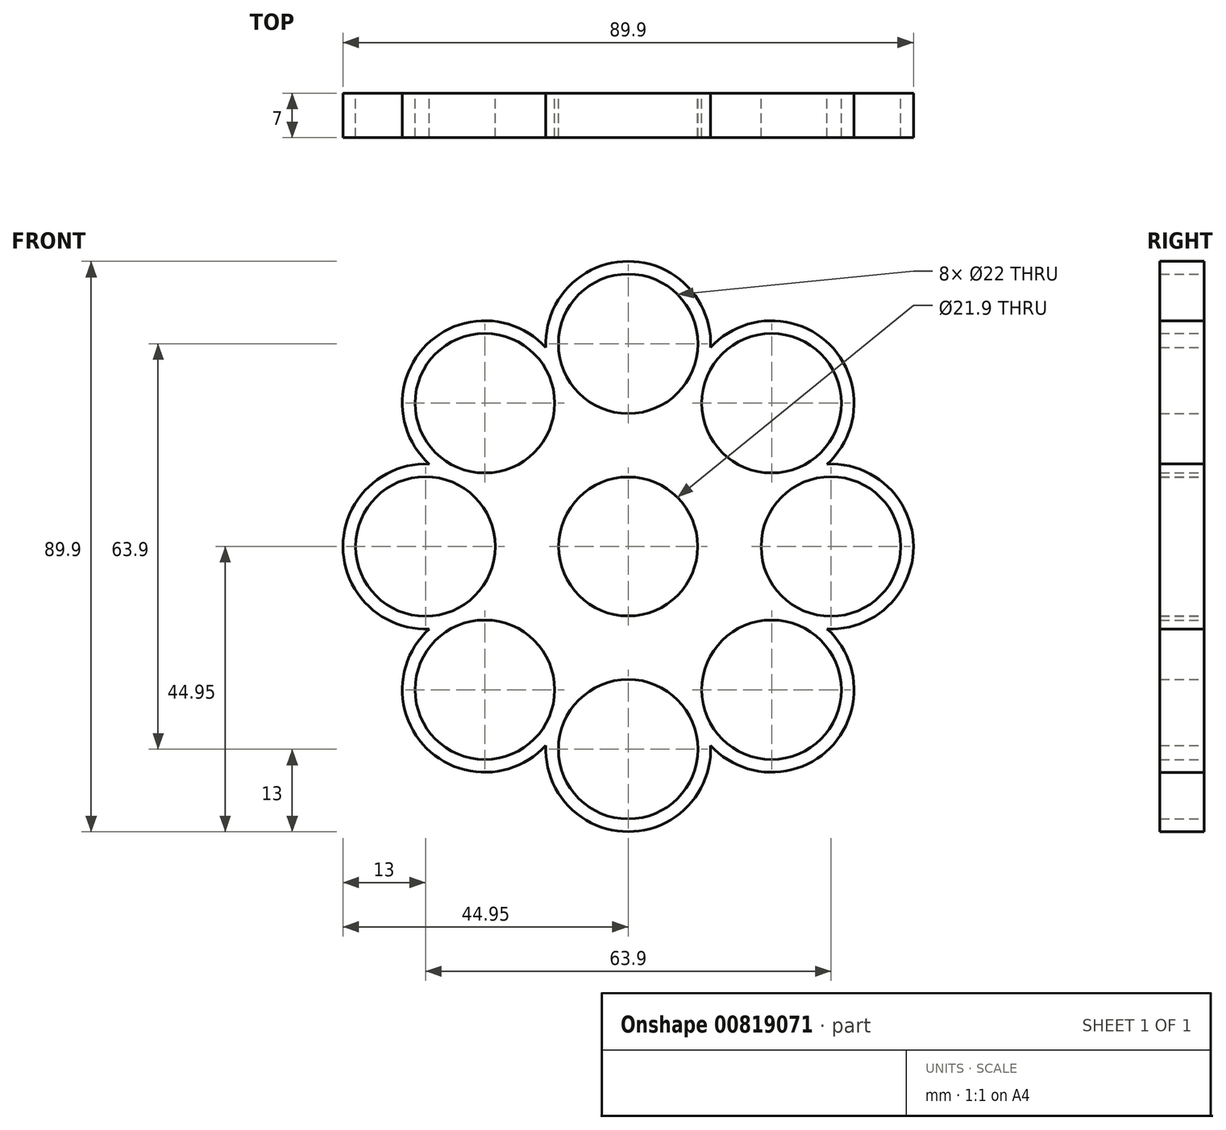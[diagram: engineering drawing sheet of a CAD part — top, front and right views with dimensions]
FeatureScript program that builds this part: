
annotation { "Feature Type Name" : "Feature", "Feature Type Description" : "" }
export const myFeature = defineFeature(function(context is Context, id is Id, definition is map)
    precondition{}
    {
        {
            var Q0;
            Q0=qCreatedBy(makeId("Front.planeOp"),FACE);
            var sketch = newSketch(context, id + "F0", { "sketchPlane" : qUnion([Q0])});
            skCircle(sketch, "E0", {"center": v(0, 0) * mm, "radius": 10.95 * mm});
            skCircle(sketch, "E1.0", {"center": v(0, 0) * mm, "radius": 12.95 * mm});
            skCircle(sketch, "E2", {"center": v(0, 31.95) * mm, "radius": 11 * mm});
            skCircle(sketch, "E3.0", {"center": v(0, 31.95) * mm, "radius": 13 * mm});
            skCircle(sketch, "E4.1.0", {"center": v(-22.6, 22.6) * mm, "radius": 11 * mm});
            skCircle(sketch, "E4.1.1", {"center": v(-22.6, 22.6) * mm, "radius": 13 * mm});
            skCircle(sketch, "E4.2.0", {"center": v(-31.95, 0) * mm, "radius": 11 * mm});
            skCircle(sketch, "E4.2.1", {"center": v(-31.95, 0) * mm, "radius": 13 * mm});
            skCircle(sketch, "E4.3.0", {"center": v(-22.6, -22.6) * mm, "radius": 11 * mm});
            skCircle(sketch, "E4.3.1", {"center": v(-22.6, -22.6) * mm, "radius": 13 * mm});
            skCircle(sketch, "E4.4.0", {"center": v(0, -31.95) * mm, "radius": 11 * mm});
            skCircle(sketch, "E4.4.1", {"center": v(0, -31.95) * mm, "radius": 13 * mm});
            skCircle(sketch, "E4.5.0", {"center": v(22.6, -22.6) * mm, "radius": 11 * mm});
            skCircle(sketch, "E4.5.1", {"center": v(22.6, -22.6) * mm, "radius": 13 * mm});
            skCircle(sketch, "E4.6.0", {"center": v(31.95, 0) * mm, "radius": 11 * mm});
            skCircle(sketch, "E4.6.1", {"center": v(31.95, 0) * mm, "radius": 13 * mm});
            skCircle(sketch, "E4.7.0", {"center": v(22.6, 22.6) * mm, "radius": 11 * mm});
            skCircle(sketch, "E4.7.1", {"center": v(22.6, 22.6) * mm, "radius": 13 * mm});
            skSolve(sketch);
        }
        {
            var Q0;
            Q0 = qSketchRegion(id + "F0", true);
            var Q1;
            Q1=makeQuery(id+"F0.imprint","IMPRINT",FACE,{"disambiguationData":[TD([[makeQuery(id+"F0.imprint","IMPRINT",EDGE,{"derivedFrom":sQuery(id+"F0.wireOp",EDGE,"E0")}),-1.0]])]});
            var Q2;
            Q2=makeQuery(id+"F0.imprint","IMPRINT",FACE,{"disambiguationData":[TD([[makeQuery(id+"F0.imprint","IMPRINT",EDGE,{"derivedFrom":sQuery(id+"F0.wireOp",EDGE,"E1.0")}),-1.0]])]});
            extrude(context, id + "F1", {"entities" : qUnion([Q0, Q1, Q2]), "depth" : 7 * mm, "offsetDistance" : 25 * mm});
        }
    });
